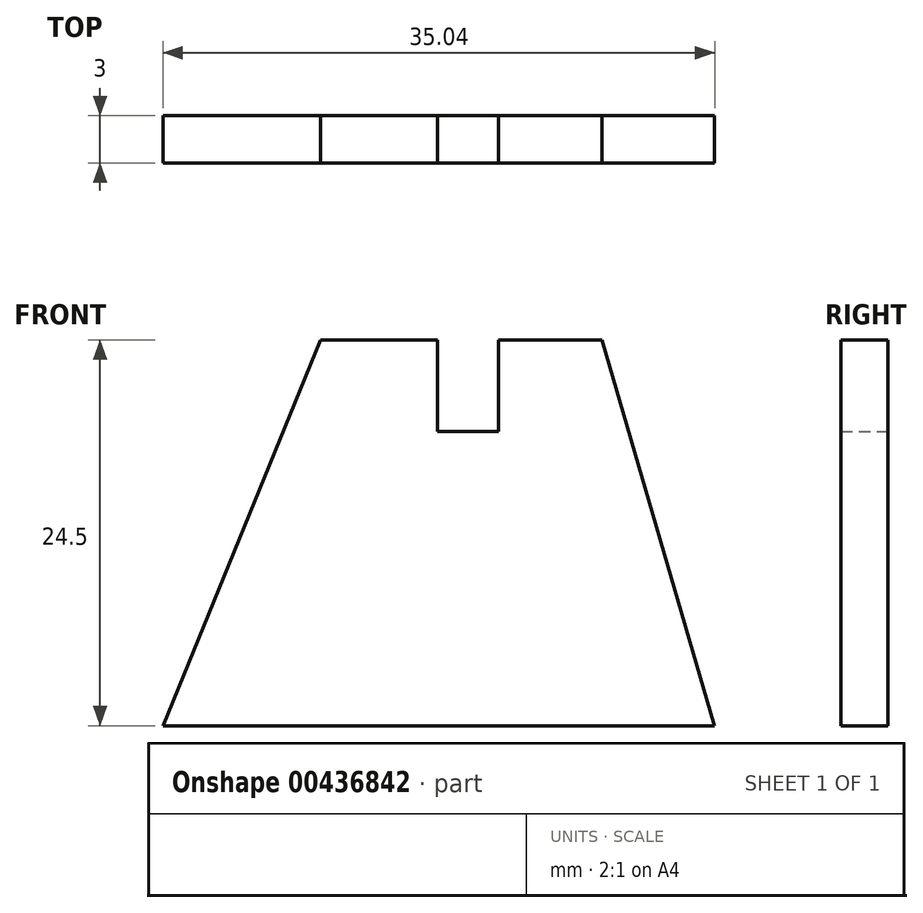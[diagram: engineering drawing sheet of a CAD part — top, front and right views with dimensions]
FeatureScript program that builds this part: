
annotation { "Feature Type Name" : "Feature", "Feature Type Description" : "" }
export const myFeature = defineFeature(function(context is Context, id is Id, definition is map)
    precondition{}
    {
        {
            var Q0;
            Q0=qCreatedBy(makeId("Front.planeOp"),FACE);
            var sketch = newSketch(context, id + "F0", { "sketchPlane" : qUnion([Q0])});
            skLineSegment(sketch, "E0", {"start": v(-53.4, 0) * mm, "end": v(-18.35, 0) * mm});
            skLineSegment(sketch, "E1", {"start": v(-18.35, 0) * mm, "end": v(-25.51, 24.5) * mm});
            skLineSegment(sketch, "E2", {"start": v(-25.51, 24.5) * mm, "end": v(-32.07, 24.5) * mm});
            skLineSegment(sketch, "E3", {"start": v(-32.07, 24.5) * mm, "end": v(-32.07, 18.69) * mm});
            skLineSegment(sketch, "E4", {"start": v(-32.07, 18.69) * mm, "end": v(-35.95, 18.69) * mm});
            skLineSegment(sketch, "E5", {"start": v(-35.95, 18.69) * mm, "end": v(-35.95, 24.5) * mm});
            skLineSegment(sketch, "E6", {"start": v(-35.95, 24.5) * mm, "end": v(-43.4, 24.5) * mm});
            skLineSegment(sketch, "E7", {"start": v(-43.4, 24.5) * mm, "end": v(-53.4, 0) * mm});
            skSolve(sketch);
        }
        {
            var Q0;
            Q0=makeQuery(id+"F0.imprint","IMPRINT",FACE,{"disambiguationData":[TD([[makeQuery(id+"F0.imprint","IMPRINT",EDGE,{"derivedFrom":sQuery(id+"F0.wireOp",EDGE,"E0")}),1.0]])]});
            extrude(context, id + "F1", {"entities" : qUnion([Q0]), "depth" : 3 * mm});
        }
    });
